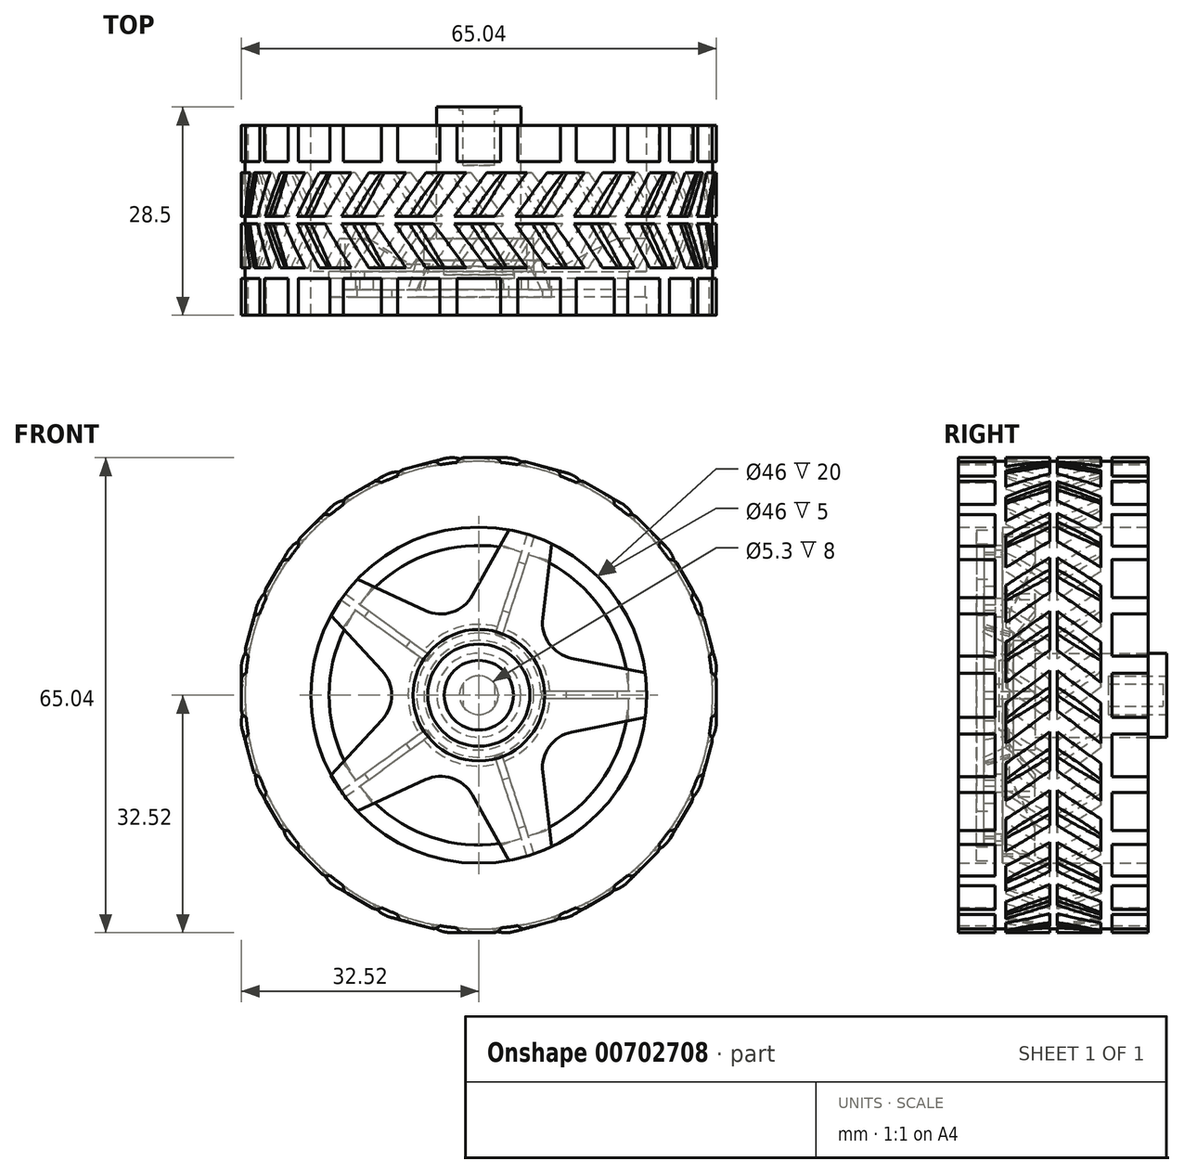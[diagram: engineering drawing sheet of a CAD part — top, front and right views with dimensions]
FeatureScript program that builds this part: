
annotation { "Feature Type Name" : "Feature", "Feature Type Description" : "" }
export const myFeature = defineFeature(function(context is Context, id is Id, definition is map)
    precondition{}
    {
        {
            var Q0;
            Q0=qCreatedBy(makeId("Top.planeOp"),FACE);
            var sketch = newSketch(context, id + "F0", { "sketchPlane" : qUnion([Q0])});
            skLineSegment(sketch, "E0", {"start": v(0, 0) * mm, "end": v(9, 0) * mm});
            skLineSegment(sketch, "E1", {"start": v(9, 0) * mm, "end": v(10, 0) * mm});
            skLineSegment(sketch, "E2", {"start": v(10, 0) * mm, "end": v(8.5, 5) * mm});
            skLineSegment(sketch, "E3", {"start": v(8.5, 5) * mm, "end": v(7.5, 5) * mm});
            skLineSegment(sketch, "E4", {"start": v(7.5, 5) * mm, "end": v(7.5, 8) * mm});
            skLineSegment(sketch, "E5", {"start": v(7.5, 8) * mm, "end": v(5.75, 8) * mm});
            skLineSegment(sketch, "E6", {"start": v(5.75, 8) * mm, "end": v(5.75, 26) * mm});
            skLineSegment(sketch, "E7", {"start": v(5.75, 26) * mm, "end": v(0, 26) * mm});
            skLineSegment(sketch, "E8", {"start": v(0, 26) * mm, "end": v(0, 0) * mm});
            skLineSegment(sketch, "E9", {"start": v(9, 0) * mm, "end": v(7, 4.2) * mm});
            skLineSegment(sketch, "E10", {"start": v(7, 4.2) * mm, "end": v(4.75, 4.2) * mm});
            skLineSegment(sketch, "E11", {"start": v(4.75, 4.2) * mm, "end": v(4.75, 3) * mm});
            skLineSegment(sketch, "E12", {"start": v(4.75, 3) * mm, "end": v(0, 3) * mm});
            skLineSegment(sketch, "E13", {"start": v(23, 0) * mm, "end": v(23, -2.5) * mm});
            skLineSegment(sketch, "E14", {"start": v(23, -2.5) * mm, "end": v(26, -2.5) * mm});
            skLineSegment(sketch, "E15", {"start": v(26, -2.5) * mm, "end": v(26, 23.5) * mm});
            skLineSegment(sketch, "E16", {"start": v(26, 23.5) * mm, "end": v(23, 23.5) * mm});
            skLineSegment(sketch, "E17", {"start": v(23, 23.5) * mm, "end": v(23, 3.5) * mm});
            skLineSegment(sketch, "E18", {"start": v(23, 3.5) * mm, "end": v(20.5, 3.5) * mm});
            skLineSegment(sketch, "E19", {"start": v(20.5, 3.5) * mm, "end": v(20.5, 2.5) * mm});
            skLineSegment(sketch, "E20", {"start": v(20.5, 2.5) * mm, "end": v(23, 2.5) * mm});
            skLineSegment(sketch, "E21", {"start": v(23, 2.5) * mm, "end": v(23, 0) * mm});
            skLineSegment(sketch, "E22", {"start": v(26, -2.5) * mm, "end": v(32, -2.5) * mm});
            skLineSegment(sketch, "E23", {"start": v(32, -2.5) * mm, "end": v(32, 23.5) * mm});
            skLineSegment(sketch, "E24", {"start": v(32, 23.5) * mm, "end": v(26, 23.5) * mm});
            skSolve(sketch);
        }
        {
            var Q0;
            Q0=makeQuery(id+"F0.imprint","IMPRINT",FACE,{"disambiguationData":[TD([[makeQuery(id+"F0.imprint","IMPRINT",EDGE,{"derivedFrom":sQuery(id+"F0.wireOp",EDGE,"E15")}),-1.0]])]});
            var Q1;
            Q1=sQuery(id+"F0.wireOp",EDGE,"E8");
            revolve(context, id + "F1", {"surfaceOperationType" : NewSurfaceOperationType.NEW, "entities" : qUnion([Q0]), "axis" : qUnion([Q1]), "revolveType" : RevolveType.FULL});
        }
        {
            var Q0;
            Q0=makeQuery(id+"F0.imprint","IMPRINT",FACE,{"disambiguationData":[TD([[makeQuery(id+"F0.imprint","IMPRINT",EDGE,{"derivedFrom":sQuery(id+"F0.wireOp",EDGE,"E13")}),1.0]])]});
            var Q1;
            Q1=makeQuery(id+"F0.imprint","IMPRINT",FACE,{"disambiguationData":[TD([[makeQuery(id+"F0.imprint","IMPRINT",EDGE,{"derivedFrom":sQuery(id+"F0.wireOp",EDGE,"E1")}),1.0]])]});
            var Q2;
            Q2=sQuery(id+"F0.wireOp",EDGE,"E8");
            revolve(context, id + "F2", {"surfaceOperationType" : NewSurfaceOperationType.NEW, "entities" : qUnion([Q0, Q1]), "axis" : qUnion([Q2]), "revolveType" : RevolveType.FULL});
        }
        {
            var Q0;
            Q0=makeQuery(id+"F2.opRevolve","SWEPT_FACE",FACE,{"disambiguationData":[OSD([sQuery(id+"F0.wireOp",EDGE,"E1")])]});
            var sketch = newSketch(context, id + "F3", { "sketchPlane" : qUnion([Q0])});
            skLineSegment(sketch, "E25", {"start": v(0, 0) * mm, "end": v(23, 0) * mm, "construction": true});
            skLineSegment(sketch, "E26", {"start": v(23, 3) * mm, "end": v(23, -3) * mm});
            skPoint(sketch, "E27", {"position": v(23, 0) * mm});
            skLineSegment(sketch, "E28", {"start": v(23, 3) * mm, "end": v(12.73, 5.05) * mm});
            skLineSegment(sketch, "E29", {"start": v(23, -3) * mm, "end": v(12.73, -5.05) * mm});
            skLineSegment(sketch, "E30.1.0", {"start": v(4.25, 22.8) * mm, "end": v(-0.88, 13.66) * mm});
            skLineSegment(sketch, "E30.1.4", {"start": v(9.96, 20.95) * mm, "end": v(8.74, 10.54) * mm});
            skLineSegment(sketch, "E30.1.5", {"start": v(4.25, 22.8) * mm, "end": v(9.96, 20.95) * mm});
            skLineSegment(sketch, "E30.2.0", {"start": v(-20.37, 11.1) * mm, "end": v(-13.27, 3.4) * mm});
            skLineSegment(sketch, "E30.2.4", {"start": v(-16.84, 15.95) * mm, "end": v(-7.32, 11.57) * mm});
            skLineSegment(sketch, "E30.2.5", {"start": v(-20.37, 11.1) * mm, "end": v(-16.84, 15.95) * mm});
            skLineSegment(sketch, "E30.3.0", {"start": v(-16.84, -15.95) * mm, "end": v(-7.32, -11.57) * mm});
            skLineSegment(sketch, "E30.3.4", {"start": v(-20.37, -11.1) * mm, "end": v(-13.27, -3.4) * mm});
            skLineSegment(sketch, "E30.3.5", {"start": v(-16.84, -15.95) * mm, "end": v(-20.37, -11.1) * mm});
            skLineSegment(sketch, "E30.4.0", {"start": v(9.96, -20.95) * mm, "end": v(8.74, -10.54) * mm});
            skLineSegment(sketch, "E30.4.4", {"start": v(4.25, -22.8) * mm, "end": v(-0.88, -13.66) * mm});
            skLineSegment(sketch, "E30.4.5", {"start": v(9.96, -20.95) * mm, "end": v(4.25, -22.8) * mm});
            skPoint(sketch, "E30.center", {"position": v(0, 0) * mm});
            skArc(sketch, "E31.filletArc", {"start": v(8.74, 10.54) * mm, "mid": v(9.66, 7.02) * mm, "end": v(12.73, 5.05) * mm});
            skArc(sketch, "E32.filletArc", {"start": v(-7.32, 11.57) * mm, "mid": v(-3.7, 11.36) * mm, "end": v(-0.88, 13.66) * mm});
            skArc(sketch, "E33.filletArc", {"start": v(-13.27, -3.4) * mm, "mid": v(-11.94, 0) * mm, "end": v(-13.27, 3.4) * mm});
            skArc(sketch, "E34.filletArc", {"start": v(-0.88, -13.66) * mm, "mid": v(-3.7, -11.36) * mm, "end": v(-7.32, -11.57) * mm});
            skArc(sketch, "E35.filletArc", {"start": v(12.73, -5.05) * mm, "mid": v(9.66, -7.02) * mm, "end": v(8.74, -10.54) * mm});
            skLineSegment(sketch, "E36", {"start": v(20.44, 3.51) * mm, "end": v(20.44, -3.51) * mm});
            skLineSegment(sketch, "E37.1.0", {"start": v(2.98, 20.53) * mm, "end": v(9.66, 18.36) * mm});
            skLineSegment(sketch, "E37.2.0", {"start": v(-18.6, 9.17) * mm, "end": v(-14.47, 14.86) * mm});
            skLineSegment(sketch, "E37.3.0", {"start": v(-14.47, -14.86) * mm, "end": v(-18.6, -9.17) * mm});
            skLineSegment(sketch, "E37.4.0", {"start": v(9.66, -18.36) * mm, "end": v(2.98, -20.53) * mm});
            skCircle(sketch, "E38", {"center": v(0, 0) * mm, "radius": 9.61 * mm});
            skSolve(sketch);
        }
        {
            var Q0;
            {var subQ0=sQuery(id+"F3.wireOp",EDGE,"E30.1.5");Q0=makeQuery(id+"F3.imprint","IMPRINT",FACE,{"disambiguationData":[TD([[makeQuery(id+"F3.imprint","IMPRINT",EDGE,{"derivedFrom":subQ0}),-1.0]])]});}
            var Q1;
            {var subQ0=sQuery(id+"F3.wireOp",EDGE,"E26");Q1=makeQuery(id+"F3.imprint","IMPRINT",FACE,{"disambiguationData":[TD([[makeQuery(id+"F3.imprint","IMPRINT",EDGE,{"derivedFrom":subQ0}),-1.0]])]});}
            var Q2;
            {var subQ0=sQuery(id+"F3.wireOp",EDGE,"E30.4.5");Q2=makeQuery(id+"F3.imprint","IMPRINT",FACE,{"disambiguationData":[TD([[makeQuery(id+"F3.imprint","IMPRINT",EDGE,{"derivedFrom":subQ0}),-1.0]])]});}
            var Q3;
            {var subQ0=sQuery(id+"F3.wireOp",EDGE,"E30.3.5");Q3=makeQuery(id+"F3.imprint","IMPRINT",FACE,{"disambiguationData":[TD([[makeQuery(id+"F3.imprint","IMPRINT",EDGE,{"derivedFrom":subQ0}),-1.0]])]});}
            var Q4;
            {var subQ0=sQuery(id+"F3.wireOp",EDGE,"E30.2.5");Q4=makeQuery(id+"F3.imprint","IMPRINT",FACE,{"disambiguationData":[TD([[makeQuery(id+"F3.imprint","IMPRINT",EDGE,{"derivedFrom":subQ0}),-1.0]])]});}
            extrude(context, id + "F4", {"entities" : qUnion([Q0, Q1, Q2, Q3, Q4]), "operationType" : NewBodyOperationType.ADD, "oppositeDirection" : true, "depth" : 3.5 * mm, "offsetDistance" : 25.4 * mm});
        }
        {
            var Q0;
            {var subQ13=sQuery(id+"F3.wireOp",EDGE,"E31.filletArc");Q0=makeQuery(id+"F3.imprint","IMPRINT",FACE,{"disambiguationData":[TD([[makeQuery(id+"F3.imprint","IMPRINT",EDGE,{"derivedFrom":subQ13}),-1.0]])]});}
            var Q1;
            Q1=makeQuery(id+"F3.imprint","IMPRINT",FACE,{"disambiguationData":[TD([[makeQuery(id+"F3.imprint","IMPRINT",EDGE,{"derivedFrom":sQuery(id+"F3.wireOp",EDGE,"E38")}),-1.0]])]});
            extrude(context, id + "F5", {"entities" : qUnion([Q0, Q1]), "operationType" : NewBodyOperationType.ADD, "oppositeDirection" : true, "depth" : 1 * mm, "offsetDistance" : 25.4 * mm});
        }
        {
            var Q0;
            Q0=qCreatedBy(makeId("Top.planeOp"),FACE);
            cPlane(context, id + "F6", {"entities" : qUnion([Q0]), "cplaneType" : CPlaneType.OFFSET, "offset" : 32.5 * mm, "width" : 152.4 * mm, "height" : 152.4 * mm});
        }
        {
            var Q0;
            Q0=qCreatedBy(id+"F6.planeOp",FACE);
            var sketch = newSketch(context, id + "F7", { "sketchPlane" : qUnion([Q0])});
            skLineSegment(sketch, "E39.bottom", {"start": v(3, -2.5) * mm, "end": v(-3, -2.5) * mm});
            skLineSegment(sketch, "E39.top", {"start": v(3, 2.5) * mm, "end": v(-3, 2.5) * mm});
            skLineSegment(sketch, "E39.left", {"start": v(3, -2.5) * mm, "end": v(3, 2.5) * mm});
            skLineSegment(sketch, "E39.right", {"start": v(-3, -2.5) * mm, "end": v(-3, 2.5) * mm});
            skLineSegment(sketch, "E40", {"start": v(2.14, 10) * mm, "end": v(-3.36, 10) * mm});
            skLineSegment(sketch, "E41", {"start": v(-3.36, 10) * mm, "end": v(1.08, 4) * mm});
            skLineSegment(sketch, "E42", {"start": v(1.08, 4) * mm, "end": v(6.58, 4) * mm});
            skLineSegment(sketch, "E43", {"start": v(6.58, 4) * mm, "end": v(2.14, 10) * mm});
            skLineSegment(sketch, "E44.MirrorCS", {"start": v(3, 23.5) * mm, "end": v(-3, 23.5) * mm});
            skLineSegment(sketch, "E45.MirrorCS", {"start": v(-3, 23.5) * mm, "end": v(-3, 18.5) * mm});
            skLineSegment(sketch, "E46.MirrorCS", {"start": v(3, 18.5) * mm, "end": v(-3, 18.5) * mm});
            skLineSegment(sketch, "E47.MirrorCS", {"start": v(3, 23.5) * mm, "end": v(3, 18.5) * mm});
            skLineSegment(sketch, "E48.MirrorCS", {"start": v(1.08, 17) * mm, "end": v(6.58, 17) * mm});
            skLineSegment(sketch, "E49.MirrorCS", {"start": v(6.58, 17) * mm, "end": v(2.14, 11) * mm});
            skLineSegment(sketch, "E50.MirrorCS", {"start": v(2.14, 11) * mm, "end": v(-3.36, 11) * mm});
            skLineSegment(sketch, "E51.MirrorCS", {"start": v(-3.36, 11) * mm, "end": v(1.08, 17) * mm});
            skSolve(sketch);
        }
        {
            var Q0;
            Q0=makeQuery(id+"F7.imprint","IMPRINT",FACE,{"disambiguationData":[TD([[makeQuery(id+"F7.imprint","IMPRINT",EDGE,{"derivedFrom":sQuery(id+"F7.wireOp",EDGE,"E44.MirrorCS")}),1.0]])]});
            var Q1;
            Q1=makeQuery(id+"F7.imprint","IMPRINT",FACE,{"disambiguationData":[TD([[makeQuery(id+"F7.imprint","IMPRINT",EDGE,{"derivedFrom":sQuery(id+"F7.wireOp",EDGE,"E48.MirrorCS")}),-1.0]])]});
            var Q2;
            Q2=makeQuery(id+"F7.imprint","IMPRINT",FACE,{"disambiguationData":[TD([[makeQuery(id+"F7.imprint","IMPRINT",EDGE,{"derivedFrom":sQuery(id+"F7.wireOp",EDGE,"E40")}),1.0]])]});
            var Q3;
            Q3=makeQuery(id+"F7.imprint","IMPRINT",FACE,{"disambiguationData":[TD([[makeQuery(id+"F7.imprint","IMPRINT",EDGE,{"derivedFrom":sQuery(id+"F7.wireOp",EDGE,"E39.bottom")}),-1.0]])]});
            extrude(context, id + "F8", {"entities" : qUnion([Q0, Q1, Q2, Q3]), "endBound" : BoundingType.UP_TO_NEXT, "oppositeDirection" : true, "depth" : 25.4 * mm, "offsetDistance" : 25.4 * mm});
        }
        {
            var Q0;
            Q0=makeQuery(id+"F8.opExtrude","CAP_EDGE",EDGE,{"disambiguationData":[OSD([sQuery(id+"F7.wireOp",EDGE,"E49.MirrorCS")])],"isStart":true});
            var Q1;
            Q1=makeQuery(id+"F8.opExtrude","CAP_EDGE",EDGE,{"disambiguationData":[OSD([sQuery(id+"F7.wireOp",EDGE,"E51.MirrorCS")])],"isStart":true});
            var Q2;
            Q2=makeQuery(id+"F8.opExtrude","CAP_EDGE",EDGE,{"disambiguationData":[OSD([sQuery(id+"F7.wireOp",EDGE,"E43")])],"isStart":true});
            var Q3;
            Q3=makeQuery(id+"F8.opExtrude","CAP_EDGE",EDGE,{"disambiguationData":[OSD([sQuery(id+"F7.wireOp",EDGE,"E41")])],"isStart":true});
            fillet(context, id + "F9", {"entities" : qUnion([Q0, Q1, Q2, Q3]), "radius" : 3 * mm, "tangentPropagation" : true, "allowEdgeOverflow" : false});
        }
        {
            var Q0;
            Q0=makeQuery(id+"F8.opExtrude","CAP_EDGE",EDGE,{"disambiguationData":[OSD([sQuery(id+"F7.wireOp",EDGE,"E39.left")])],"isStart":true});
            var Q1;
            Q1=makeQuery(id+"F8.opExtrude","CAP_EDGE",EDGE,{"disambiguationData":[OSD([sQuery(id+"F7.wireOp",EDGE,"E39.right")])],"isStart":true});
            var Q2;
            Q2=makeQuery(id+"F8.opExtrude","CAP_EDGE",EDGE,{"disambiguationData":[OSD([sQuery(id+"F7.wireOp",EDGE,"E45.MirrorCS")])],"isStart":true});
            var Q3;
            Q3=makeQuery(id+"F8.opExtrude","CAP_EDGE",EDGE,{"disambiguationData":[OSD([sQuery(id+"F7.wireOp",EDGE,"E47.MirrorCS")])],"isStart":true});
            fillet(context, id + "F10", {"entities" : qUnion([Q0, Q1, Q2, Q3]), "radius" : 1 * mm, "tangentPropagation" : true, "allowEdgeOverflow" : false});
        }
        {
            var Q0;
            Q0=makeQuery(id+"F8.opExtrude","SWEPT_BODY",BODY,{"disambiguationData":[OSD([sQuery(id+"F7.wireOp",EDGE,"E39.bottom"),sQuery(id+"F7.wireOp",EDGE,"E39.top"),sQuery(id+"F7.wireOp",EDGE,"E39.left"),sQuery(id+"F7.wireOp",EDGE,"E39.right")])]});
            var Q1;
            Q1=makeQuery(id+"F8.opExtrude","SWEPT_BODY",BODY,{"disambiguationData":[OSD([sQuery(id+"F7.wireOp",EDGE,"E40"),sQuery(id+"F7.wireOp",EDGE,"E41"),sQuery(id+"F7.wireOp",EDGE,"E42"),sQuery(id+"F7.wireOp",EDGE,"E43")])]});
            var Q2;
            Q2=makeQuery(id+"F8.opExtrude","SWEPT_BODY",BODY,{"disambiguationData":[OSD([sQuery(id+"F7.wireOp",EDGE,"E48.MirrorCS"),sQuery(id+"F7.wireOp",EDGE,"E49.MirrorCS"),sQuery(id+"F7.wireOp",EDGE,"E50.MirrorCS"),sQuery(id+"F7.wireOp",EDGE,"E51.MirrorCS")])]});
            var Q3;
            Q3=makeQuery(id+"F8.opExtrude","SWEPT_BODY",BODY,{"disambiguationData":[OSD([sQuery(id+"F7.wireOp",EDGE,"E44.MirrorCS"),sQuery(id+"F7.wireOp",EDGE,"E45.MirrorCS"),sQuery(id+"F7.wireOp",EDGE,"E46.MirrorCS"),sQuery(id+"F7.wireOp",EDGE,"E47.MirrorCS")])]});
            var Q4;
            Q4=sQuery(id+"F0.wireOp",EDGE,"E8");
            circularPattern(context, id + "F11", {"operationType" : NewBodyOperationType.ADD, "entities" : qUnion([Q0, Q1, Q2, Q3]), "axis" : qUnion([Q4]), "angle" : 360 * degree, "instanceCount" : 24, "equalSpace" : true});
        }
        {
            var Q0;
            Q0=makeQuery(id+"F2.opRevolve","SWEPT_FACE",FACE,{"disambiguationData":[OSD([sQuery(id+"F0.wireOp",EDGE,"E7")])]});
            var sketch = newSketch(context, id + "F12", { "sketchPlane" : qUnion([Q0])});
            skLineSegment(sketch, "E52.0", {"start": v(2.16, 1.53) * mm, "end": v(2.16, -1.53) * mm});
            skLineSegment(sketch, "E53.0", {"start": v(-2.16, 1.53) * mm, "end": v(-2.16, -1.53) * mm});
            skCircle(sketch, "E54", {"center": v(0, 0) * mm, "radius": 2.65 * mm});
            skSolve(sketch);
        }
        {
            var Q0;
            {var subQ0=sQuery(id+"F12.wireOp",EDGE,"E52.0");Q0=makeQuery(id+"F12.imprint","IMPRINT",FACE,{"disambiguationData":[TD([[makeQuery(id+"F12.imprint","IMPRINT",EDGE,{"derivedFrom":subQ0}),-1.0]])]});}
            extrude(context, id + "F13", {"entities" : qUnion([Q0]), "operationType" : NewBodyOperationType.REMOVE, "oppositeDirection" : true, "depth" : 8 * mm, "offsetDistance" : 25.4 * mm});
        }
        {
            var Q0;
            {var subQ0=sQuery(id+"F12.wireOp",EDGE,"E52.0");Q0=makeQuery(id+"F12.imprint","IMPRINT",FACE,{"disambiguationData":[TD([[makeQuery(id+"F12.imprint","IMPRINT",EDGE,{"derivedFrom":subQ0}),1.0]])]});}
            var Q1;
            {var subQ0=sQuery(id+"F12.wireOp",EDGE,"E53.0");Q1=makeQuery(id+"F12.imprint","IMPRINT",FACE,{"disambiguationData":[TD([[makeQuery(id+"F12.imprint","IMPRINT",EDGE,{"derivedFrom":subQ0}),-1.0]])]});}
            extrude(context, id + "F14", {"entities" : qUnion([Q0, Q1]), "operationType" : NewBodyOperationType.REMOVE, "oppositeDirection" : true, "depth" : 0.5 * mm, "offsetDistance" : 25.4 * mm});
        }
        {
            var Q0;
            Q0=qCreatedBy(makeId("Top.planeOp"),FACE);
            cPlane(context, id + "F15", {"entities" : qUnion([Q0]), "cplaneType" : CPlaneType.OFFSET, "offset" : 0.5 * mm, "width" : 152.4 * mm, "height" : 152.4 * mm});
        }
        {
            var Q0;
            Q0=qCreatedBy(id+"F15.planeOp",FACE);
            var sketch = newSketch(context, id + "F16", { "sketchPlane" : qUnion([Q0])});
            skLineSegment(sketch, "E55", {"start": v(0, 0) * mm, "end": v(26, 0) * mm});
            skLineSegment(sketch, "E56", {"start": v(26, 0) * mm, "end": v(26, 8) * mm});
            skLineSegment(sketch, "E57", {"start": v(26, 8) * mm, "end": v(19, 8) * mm});
            skLineSegment(sketch, "E58", {"start": v(19, 8) * mm, "end": v(12, 4.5) * mm});
            skLineSegment(sketch, "E59", {"start": v(12, 4.5) * mm, "end": v(9.5, 4.5) * mm});
            skLineSegment(sketch, "E60", {"start": v(10, 0) * mm, "end": v(7.1, 4.5) * mm});
            skLineSegment(sketch, "E61", {"start": v(7.1, 4.5) * mm, "end": v(9.5, 4.5) * mm});
            skSolve(sketch);
        }
        {
            var Q0;
            {var subQ0=sQuery(id+"F16.wireOp",EDGE,"E56");Q0=makeQuery(id+"F16.imprint","IMPRINT",FACE,{"disambiguationData":[TD([[makeQuery(id+"F16.imprint","IMPRINT",EDGE,{"derivedFrom":subQ0}),1.0]])]});}
            extrude(context, id + "F17", {"entities" : qUnion([Q0]), "oppositeDirection" : true, "depth" : 1 * mm, "offsetDistance" : 25.4 * mm});
        }
        {
            var Q0;
            Q0=makeQuery(id+"F17.opExtrude","SWEPT_BODY",BODY,{"disambiguationData":[OSD([sQuery(id+"F16.wireOp",EDGE,"E55"),sQuery(id+"F16.wireOp",EDGE,"E56"),sQuery(id+"F16.wireOp",EDGE,"E57"),sQuery(id+"F16.wireOp",EDGE,"E58"),sQuery(id+"F16.wireOp",EDGE,"E59"),sQuery(id+"F16.wireOp",EDGE,"E60"),sQuery(id+"F16.wireOp",EDGE,"E61")])]});
            var Q1;
            Q1=sQuery(id+"F0.wireOp",EDGE,"E8");
            circularPattern(context, id + "F18", {"operationType" : NewBodyOperationType.ADD, "entities" : qUnion([Q0]), "axis" : qUnion([Q1]), "angle" : 360 * degree, "instanceCount" : 5, "equalSpace" : true});
        }
    });
